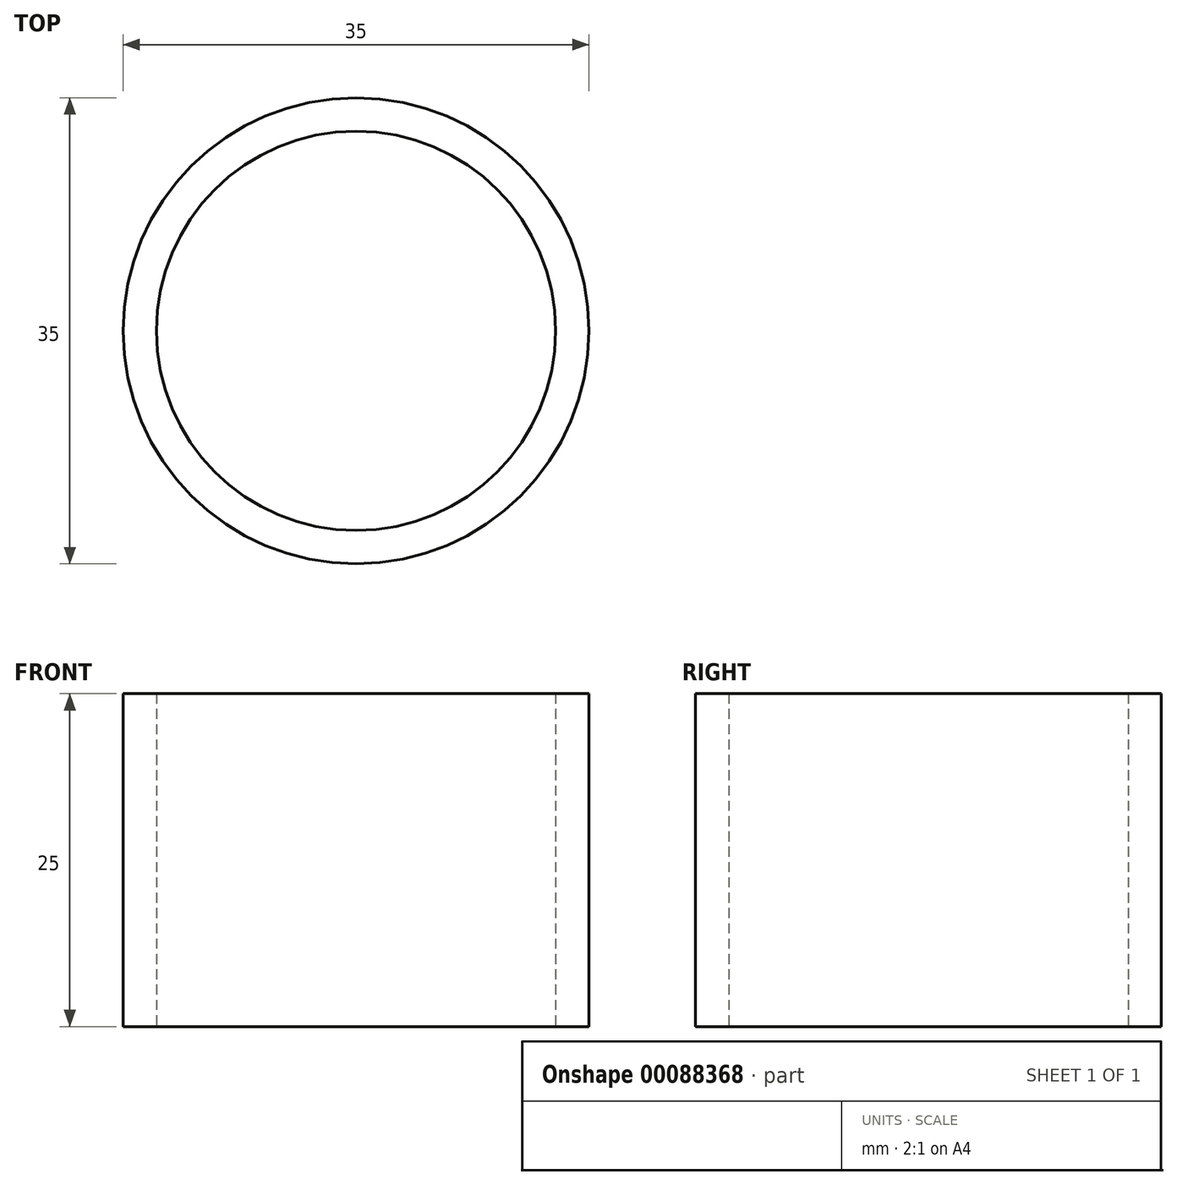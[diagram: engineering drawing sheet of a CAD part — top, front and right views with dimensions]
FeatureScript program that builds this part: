
annotation { "Feature Type Name" : "Feature", "Feature Type Description" : "" }
export const myFeature = defineFeature(function(context is Context, id is Id, definition is map)
    precondition{}
    {
        {
            var Q0;
            Q0=qCreatedBy(makeId("Top.planeOp"),FACE);
            var sketch = newSketch(context, id + "F0", { "sketchPlane" : qUnion([Q0])});
            skCircle(sketch, "E0", {"center": v(0, 0) * mm, "radius": 15 * mm});
            skCircle(sketch, "E1.0", {"center": v(0, 0) * mm, "radius": 17.5 * mm});
            skSolve(sketch);
        }
        {
            var Q0;
            Q0 = qSketchRegion(id + "F0", true);
            extrude(context, id + "F1", {"entities" : qUnion([Q0]), "depth" : 25 * mm});
        }
    });
